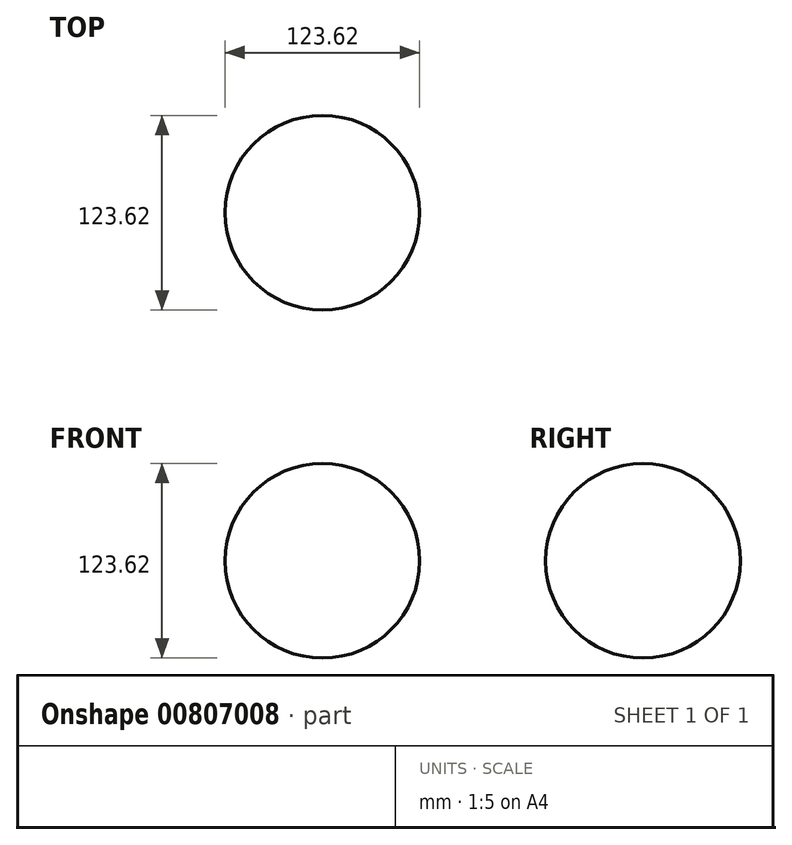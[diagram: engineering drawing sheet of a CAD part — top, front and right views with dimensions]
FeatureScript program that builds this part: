
annotation { "Feature Type Name" : "Feature", "Feature Type Description" : "" }
export const myFeature = defineFeature(function(context is Context, id is Id, definition is map)
    precondition{}
    {
        {
            var Q0;
            Q0=qCreatedBy(makeId("Front.planeOp"),FACE);
            var sketch = newSketch(context, id + "F0", { "sketchPlane" : qUnion([Q0])});
            skCircle(sketch, "E0", {"center": v(0, 0) * mm, "radius": 61.81 * mm});
            skLineSegment(sketch, "E1", {"start": v(0, 0) * mm, "end": v(0, 66.42) * mm});
            skLineSegment(sketch, "E2", {"start": v(0, 0) * mm, "end": v(0, -98) * mm});
            skSolve(sketch);
        }
        {
            var Q0;
            {var subQ0=sQuery(id+"F0.wireOp",EDGE,"E1");var subQ1=sQuery(id+"F0.wireOp",EDGE,"E0");var subQ2=makeQuery(id+"F0.imprint","INTERSECT",VERTEX,{"derivedFrom":[subQ1,subQ0]});Q0=makeQuery(id+"F0.imprint","IMPRINT",FACE,{"disambiguationData":[TD([[makeQuery(id+"F0.imprint","IMPRINT",EDGE,{"disambiguationData":[TD([[subQ2,1.0]])],"derivedFrom":subQ1}),1.0]])]});}
            var Q1;
            Q1=sQuery(id+"F0.wireOp",EDGE,"E2");
            revolve(context, id + "F1", {"surfaceOperationType" : NewSurfaceOperationType.NEW, "entities" : qUnion([Q0]), "axis" : qUnion([Q1]), "revolveType" : RevolveType.FULL});
        }
    });
